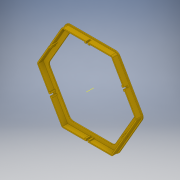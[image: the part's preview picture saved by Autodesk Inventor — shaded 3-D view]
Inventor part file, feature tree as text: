
AUTODESK INVENTOR PART (.ipt)
format: ipt  version: 2019 (Build 230136000, 136)  size: 522,752 bytes
history: native  units: mm
features: extrude x5, sketch x5, projected_geometry x3, fillet x2, other x1, pattern_circular x1
ambient origin geometry x8: Origin, YZ Plane, XZ Plane, XY Plane, X Axis, Y Axis, Z Axis, Center Point
bodies: Solid1 (feature_tree)
feature tree (17):
  extrude  "Extrusion1"  Depth=2.0mm
  extrude  "Extrusion5"  Depth=2.0mm
  extrude  "Extrusion6"  Depth=10.0mm
  fillet  "Fillet1"  [1 undecoded]
  fillet  "Fillet2"  Radius=8.0mm
  extrude  "Extrusion7"  TaperAngle=0.0deg  [1 undecoded]
  extrude  "Extrusion8"  Depth=4.0mm
  other  "Work Axis2"
  pattern_circular  "Circular Pattern1"  [2 undecoded]
  sketch  "Sketch1"  dims[d0=175.0mm d1=2.0mm]
  sketch  "Sketch5"  dims[d2=0.0mm d15=2.0mm]
  projected_geometry  "Projected Loop4"
  sketch  "Sketch7"  dims[d16=2.0mm d17=10.0mm d18=0.0mm d19=8.0mm]
  projected_geometry  "Projected Loop6"
  sketch  "Sketch8"  dims[d20=7.0mm d21=0.0mm]
  sketch  "Sketch9"  dims[d22=10.0mm d23=4.0mm d24=10.0mm d25=3.3mm d26=7.0mm d27=0.0mm d28=4.0mm d29=3.0mm d30=5.0mm d31=0.0mm d32=60.0mm d33=360.0deg]
  projected_geometry  "Projected Loop7"
note: 4 required parameter values undecoded (feature->parameter linkage not recoverable at this tier; creation-order binding heuristic only, values carry confidence <= 0.55)
